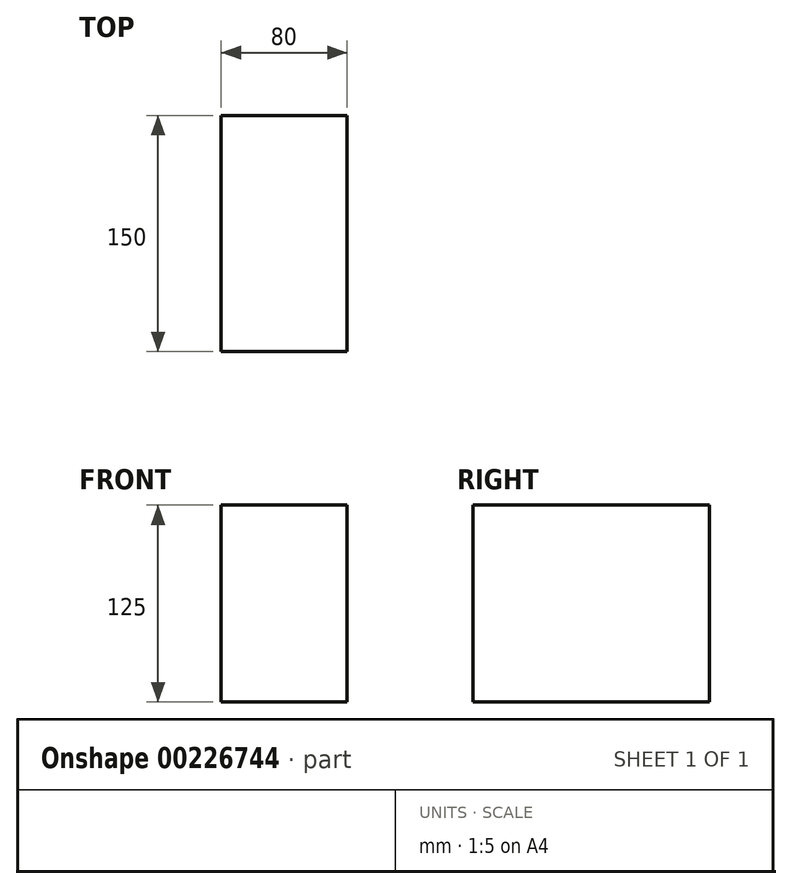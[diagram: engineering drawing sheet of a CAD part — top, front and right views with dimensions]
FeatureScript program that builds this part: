
annotation { "Feature Type Name" : "Feature", "Feature Type Description" : "" }
export const myFeature = defineFeature(function(context is Context, id is Id, definition is map)
    precondition{}
    {
        {
            var Q0;
            Q0=qCreatedBy(makeId("Front.planeOp"),FACE);
            var sketch = newSketch(context, id + "F0", { "sketchPlane" : qUnion([Q0])});
            skLineSegment(sketch, "E0.bottom", {"start": v(-40, 62.5) * mm, "end": v(40, 62.5) * mm});
            skLineSegment(sketch, "E0.top", {"start": v(-40, -62.5) * mm, "end": v(40, -62.5) * mm});
            skLineSegment(sketch, "E0.left", {"start": v(-40, 62.5) * mm, "end": v(-40, -62.5) * mm});
            skLineSegment(sketch, "E0.right", {"start": v(40, 62.5) * mm, "end": v(40, -62.5) * mm});
            skPoint(sketch, "E0.middle", {"position": v(0, 0) * mm});
            skSolve(sketch);
        }
        {
            var Q0;
            Q0=makeQuery(id+"F0.imprint","IMPRINT",FACE,{"disambiguationData":[TD([[makeQuery(id+"F0.imprint","IMPRINT",EDGE,{"derivedFrom":sQuery(id+"F0.wireOp",EDGE,"E0.bottom")}),-1.0]])]});
            extrude(context, id + "F1", {"entities" : qUnion([Q0]), "depth" : 150 * mm});
        }
    });
